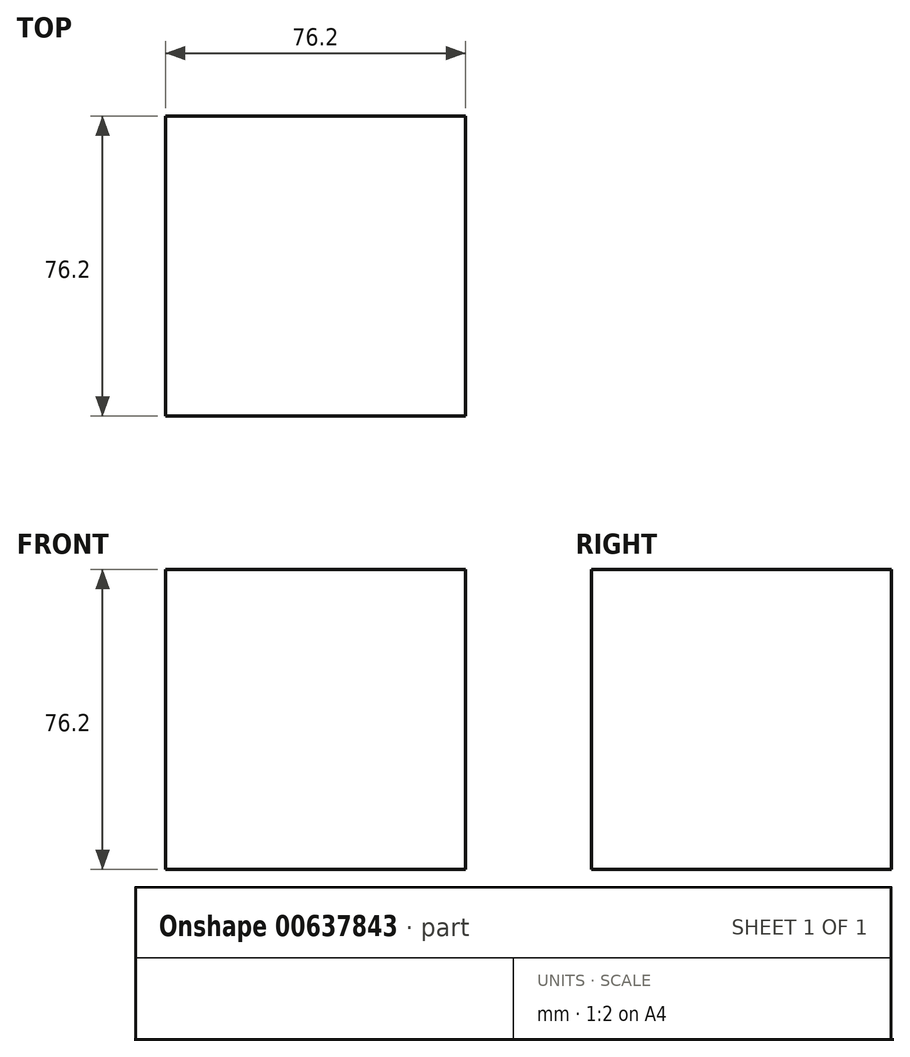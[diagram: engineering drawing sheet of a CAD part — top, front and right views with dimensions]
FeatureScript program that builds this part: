
annotation { "Feature Type Name" : "Feature", "Feature Type Description" : "" }
export const myFeature = defineFeature(function(context is Context, id is Id, definition is map)
    precondition{}
    {
        {
            var Q0;
            Q0=qCreatedBy(makeId("Front.planeOp"),FACE);
            var sketch = newSketch(context, id + "F0", { "sketchPlane" : qUnion([Q0])});
            skLineSegment(sketch, "E0.bottom", {"start": v(0, 0) * mm, "end": v(76.2, 0) * mm});
            skLineSegment(sketch, "E0.top", {"start": v(0, 76.2) * mm, "end": v(76.2, 76.2) * mm});
            skLineSegment(sketch, "E0.left", {"start": v(0, 0) * mm, "end": v(0, 76.2) * mm});
            skLineSegment(sketch, "E0.right", {"start": v(76.2, 0) * mm, "end": v(76.2, 76.2) * mm});
            skSolve(sketch);
        }
        {
            var Q0;
            Q0 = qSketchRegion(id + "F0", true);
            extrude(context, id + "F1", {"entities" : qUnion([Q0]), "depth" : 76.2 * mm, "offsetDistance" : 25.4 * mm});
        }
    });
